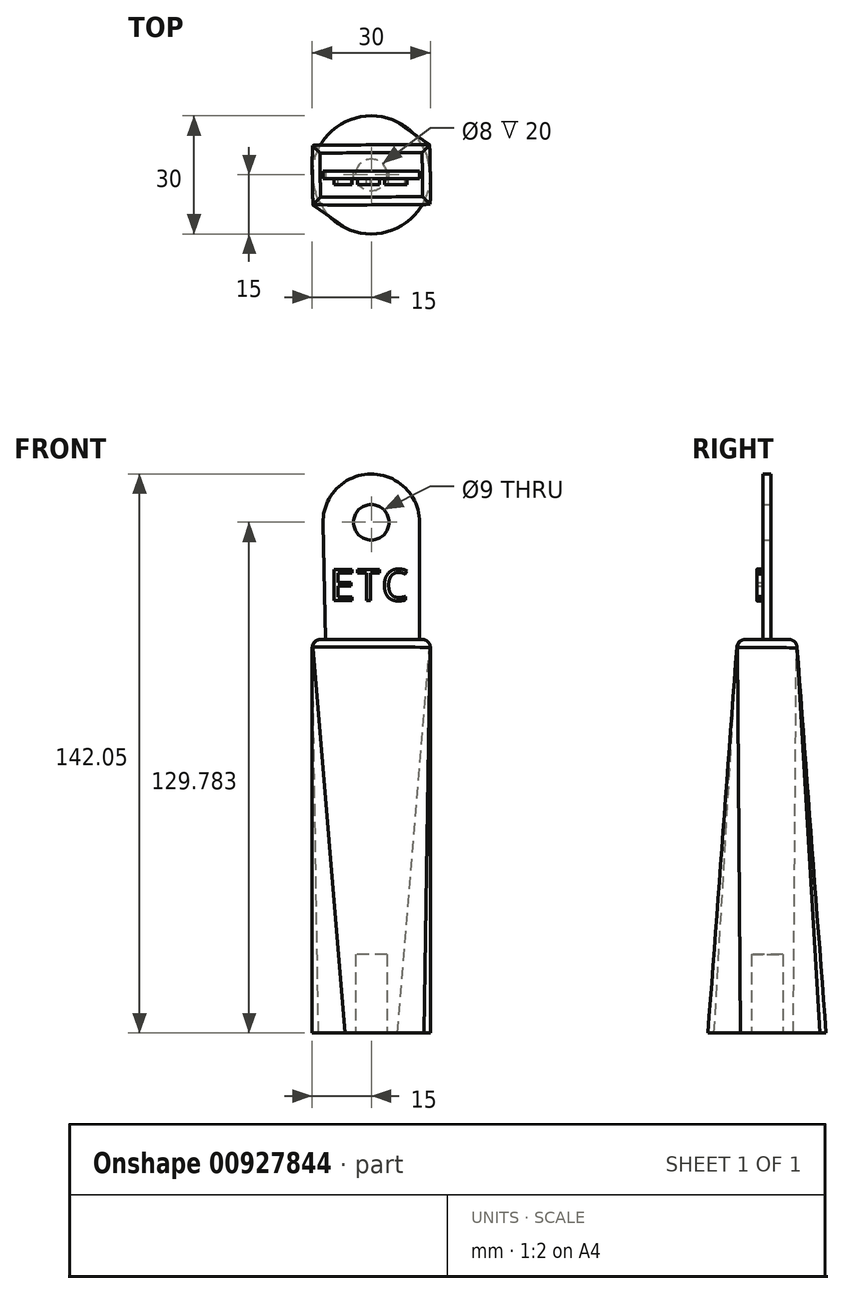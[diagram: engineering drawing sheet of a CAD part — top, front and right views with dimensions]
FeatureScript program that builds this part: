
annotation { "Feature Type Name" : "Feature", "Feature Type Description" : "" }
export const myFeature = defineFeature(function(context is Context, id is Id, definition is map)
    precondition{}
    {
        {
            var Q0;
            Q0=qCreatedBy(makeId("Top.planeOp"),FACE);
            var sketch = newSketch(context, id + "F0", { "sketchPlane" : qUnion([Q0])});
            skCircle(sketch, "E0", {"center": v(0, 0) * mm, "radius": 15 * mm});
            skSolve(sketch);
        }
        {
            var Q0;
            Q0=qCreatedBy(makeId("Top.planeOp"),FACE);
            cPlane(context, id + "F1", {"entities" : qUnion([Q0]), "cplaneType" : CPlaneType.OFFSET, "offset" : 100 * mm, "width" : 150 * mm, "height" : 150 * mm});
        }
        {
            var Q0;
            Q0=qCreatedBy(id+"F1.planeOp",FACE);
            var sketch = newSketch(context, id + "F2", { "sketchPlane" : qUnion([Q0])});
            skLineSegment(sketch, "E1.bottom", {"start": v(15, -7.5) * mm, "end": v(-15, -7.5) * mm});
            skLineSegment(sketch, "E1.top", {"start": v(15, 7.5) * mm, "end": v(-15, 7.5) * mm});
            skLineSegment(sketch, "E1.left", {"start": v(15, -7.5) * mm, "end": v(15, 7.5) * mm});
            skLineSegment(sketch, "E1.right", {"start": v(-15, -7.5) * mm, "end": v(-15, 7.5) * mm});
            skPoint(sketch, "E1.middle", {"position": v(0, 0) * mm});
            skSolve(sketch);
        }
        {
            var Q0;
            Q0=makeQuery(id+"F0.imprint","IMPRINT",FACE,{"disambiguationData":[TD([[makeQuery(id+"F0.imprint","IMPRINT",EDGE,{"derivedFrom":sQuery(id+"F0.wireOp",EDGE,"E0")}),1.0]])]});
            var Q1;
            Q1=makeQuery(id+"F2.imprint","IMPRINT",FACE,{"disambiguationData":[TD([[makeQuery(id+"F2.imprint","IMPRINT",EDGE,{"derivedFrom":sQuery(id+"F2.wireOp",EDGE,"E1.bottom")}),-1.0]])]});
            loft(context, id + "F3", {"sheetProfilesArray" : [{ "sheetProfileEntities" : qUnion([Q0]) }, { "sheetProfileEntities" : qUnion([Q1]) }]});
        }
        {
            var Q0;
            Q0=makeQuery(id+"F3.opLoft","CAP_FACE",FACE,{"disambiguationData":[OSD([makeQuery(id+"F2.imprint","IMPRINT",FACE,{"disambiguationData":[TD([[makeQuery(id+"F2.imprint","IMPRINT",EDGE,{"derivedFrom":sQuery(id+"F2.wireOp",EDGE,"E1.bottom")}),-1.0]])]})])],"isStart":true});
            fillet(context, id + "F4", {"entities" : qUnion([Q0]), "radius" : 2 * mm, "tangentPropagation" : true, "allowEdgeOverflow" : false});
        }
        {
            var Q0;
            Q0=qCreatedBy(makeId("Top.planeOp"),FACE);
            var sketch = newSketch(context, id + "F5", { "sketchPlane" : qUnion([Q0])});
            skCircle(sketch, "E2", {"center": v(0, 0) * mm, "radius": 4 * mm});
            skSolve(sketch);
        }
        {
            var Q0;
            Q0=makeQuery(id+"F5.imprint","IMPRINT",FACE,{"disambiguationData":[TD([[makeQuery(id+"F5.imprint","IMPRINT",EDGE,{"derivedFrom":sQuery(id+"F5.wireOp",EDGE,"E2")}),1.0]])]});
            var Q1;
            Q1=sQuery(id+"F5.wireOp",EDGE,"E2");
            extrude(context, id + "F6", {"entities" : qUnion([Q0]), "operationType" : NewBodyOperationType.REMOVE, "surfaceEntities" : qUnion([Q1]), "depth" : 20 * mm, "offsetDistance" : 25 * mm});
        }
        {
            var Q0;
            Q0=qCreatedBy(makeId("Front.planeOp"),FACE);
            var sketch = newSketch(context, id + "F7", { "sketchPlane" : qUnion([Q0])});
            skCircle(sketch, "E3", {"center": v(0, 129.78) * mm, "radius": 4.5 * mm});
            skCircle(sketch, "E4", {"center": v(0, 129.78) * mm, "radius": 12.27 * mm});
            skLineSegment(sketch, "E5", {"start": v(12.27, 129.78) * mm, "end": v(12.27, 97.89) * mm});
            skLineSegment(sketch, "E6", {"start": v(12.27, 97.89) * mm, "end": v(-11.65, 97.89) * mm});
            skLineSegment(sketch, "E7", {"start": v(-11.65, 97.89) * mm, "end": v(-12.27, 129.78) * mm});
            skSolve(sketch);
        }
        {
            var Q0;
            {var subQ0=sQuery(id+"F7.wireOp",EDGE,"E5");Q0=makeQuery(id+"F7.imprint","IMPRINT",FACE,{"disambiguationData":[TD([[makeQuery(id+"F7.imprint","IMPRINT",EDGE,{"derivedFrom":subQ0}),-1.0]])]});}
            var Q1;
            Q1=makeQuery(id+"F7.imprint","IMPRINT",FACE,{"disambiguationData":[TD([[makeQuery(id+"F7.imprint","IMPRINT",EDGE,{"derivedFrom":sQuery(id+"F7.wireOp",EDGE,"E3")}),-1.0]])]});
            extrude(context, id + "F8", {"entities" : qUnion([Q0, Q1]), "operationType" : NewBodyOperationType.ADD, "endBound" : BoundingType.SYMMETRIC, "depth" : 2 * mm, "offsetDistance" : 25 * mm});
        }
        {
            var Q0;
            Q0=makeQuery(id+"F8.opExtrude","CAP_FACE",FACE,{"disambiguationData":[OSD([sQuery(id+"F7.wireOp",EDGE,"E3"),sQuery(id+"F7.wireOp",EDGE,"E4"),sQuery(id+"F7.wireOp",EDGE,"E5"),sQuery(id+"F7.wireOp",EDGE,"E6"),sQuery(id+"F7.wireOp",EDGE,"E7")])],"isStart":false});
            var sketch = newSketch(context, id + "F9", { "sketchPlane" : qUnion([Q0])});
            skText(sketch, "E8", { "text": "ETC", "fontName": "DroidSansMono.ttf"});
            const initialGuessF9  = {"E8": [-0.0107, 0.10988, 1, 0, 0.008]};
            skSetInitialGuess(sketch, initialGuessF9);
            skSolve(sketch);
        }
        {
            var Q0;
            Q0=qSketchRegion(id+"F9",true);
            extrude(context, id + "F10", {"entities" : qUnion([Q0]), "operationType" : NewBodyOperationType.ADD, "depth" : 1.5 * mm, "offsetDistance" : 25 * mm});
        }
    });
